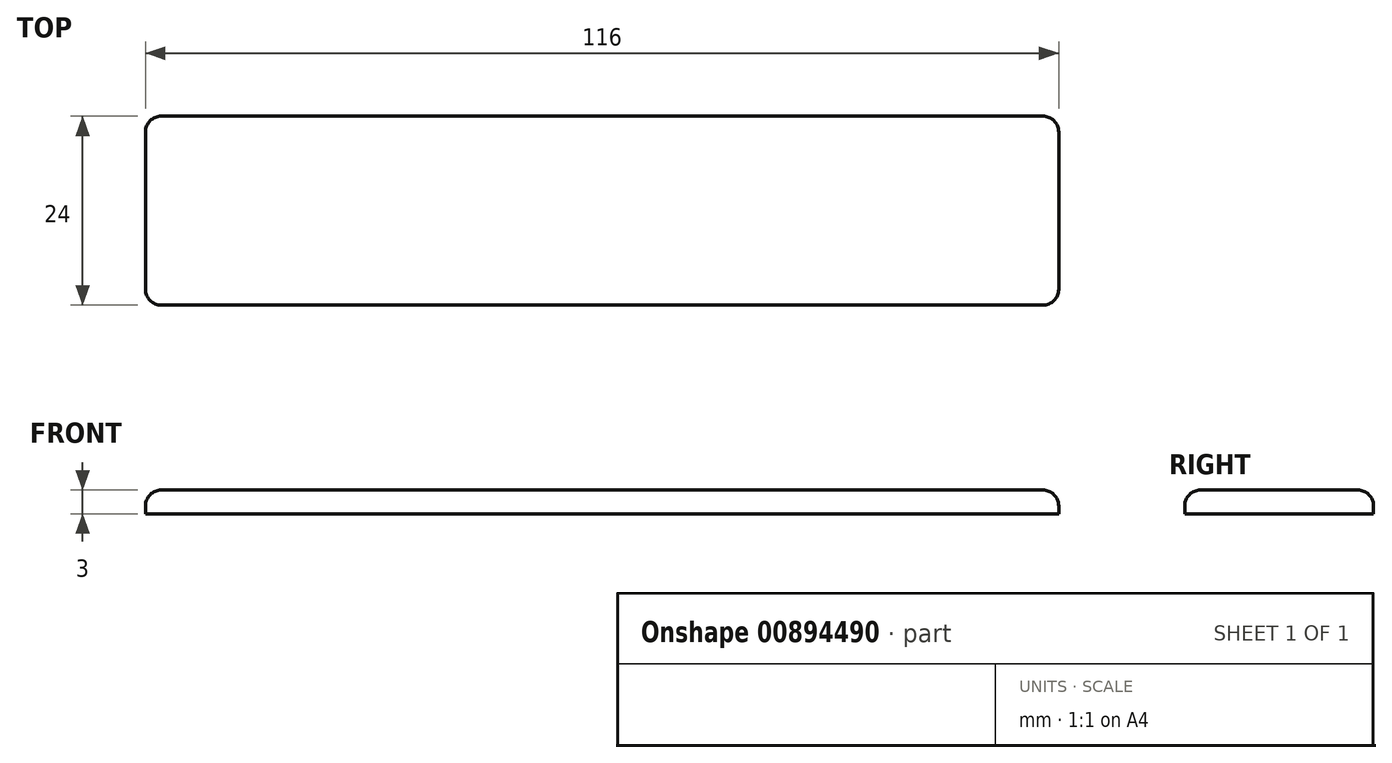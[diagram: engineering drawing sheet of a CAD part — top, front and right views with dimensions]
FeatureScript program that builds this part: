
annotation { "Feature Type Name" : "Feature", "Feature Type Description" : "" }
export const myFeature = defineFeature(function(context is Context, id is Id, definition is map)
    precondition{}
    {
        {
            var Q0;
            Q0=qCreatedBy(makeId("Top.planeOp"),FACE);
            var sketch = newSketch(context, id + "F0", { "sketchPlane" : qUnion([Q0])});
            skLineSegment(sketch, "E0.bottom", {"start": v(58, 12) * mm, "end": v(-58, 12) * mm});
            skLineSegment(sketch, "E0.top", {"start": v(58, -12) * mm, "end": v(-58, -12) * mm});
            skLineSegment(sketch, "E0.left", {"start": v(58, 12) * mm, "end": v(58, -12) * mm});
            skLineSegment(sketch, "E0.right", {"start": v(-58, 12) * mm, "end": v(-58, -12) * mm});
            skPoint(sketch, "E0.middle", {"position": v(0, 0) * mm});
            skSolve(sketch);
        }
        {
            var Q0;
            Q0=makeQuery(id+"F0.imprint","IMPRINT",FACE,{"disambiguationData":[TD([[makeQuery(id+"F0.imprint","IMPRINT",EDGE,{"derivedFrom":sQuery(id+"F0.wireOp",EDGE,"E0.bottom")}),1.0]])]});
            extrude(context, id + "F1", {"entities" : qUnion([Q0]), "depth" : 3 * mm, "offsetDistance" : 25 * mm});
        }
        {
            var Q0;
            Q0=makeQuery(id+"F1.opExtrude","CAP_FACE",FACE,{"disambiguationData":[OSD([sQuery(id+"F0.wireOp",EDGE,"E0.bottom"),sQuery(id+"F0.wireOp",EDGE,"E0.top"),sQuery(id+"F0.wireOp",EDGE,"E0.left"),sQuery(id+"F0.wireOp",EDGE,"E0.right")])],"isStart":false});
            fillet(context, id + "F2", {"entities" : qUnion([Q0]), "radius" : 2 * mm, "tangentPropagation" : true, "allowEdgeOverflow" : false});
        }
        {
            var Q0;
            Q0=makeQuery(id+"F1.opExtrude","SWEPT_EDGE",EDGE,{"disambiguationData":[OSD([sQuery(id+"F0.wireOp",EDGE,"E0.top"),sQuery(id+"F0.wireOp",EDGE,"E0.left")])]});
            var Q1;
            Q1=makeQuery(id+"F1.opExtrude","SWEPT_EDGE",EDGE,{"disambiguationData":[OSD([sQuery(id+"F0.wireOp",EDGE,"E0.bottom"),sQuery(id+"F0.wireOp",EDGE,"E0.left")])]});
            var Q2;
            Q2=makeQuery(id+"F1.opExtrude","SWEPT_EDGE",EDGE,{"disambiguationData":[OSD([sQuery(id+"F0.wireOp",EDGE,"E0.top"),sQuery(id+"F0.wireOp",EDGE,"E0.right")])]});
            var Q3;
            Q3=makeQuery(id+"F1.opExtrude","SWEPT_EDGE",EDGE,{"disambiguationData":[OSD([sQuery(id+"F0.wireOp",EDGE,"E0.bottom"),sQuery(id+"F0.wireOp",EDGE,"E0.right")])]});
            fillet(context, id + "F3", {"entities" : qUnion([Q0, Q1, Q2, Q3]), "radius" : 2 * mm, "tangentPropagation" : true, "allowEdgeOverflow" : false});
        }
    });
